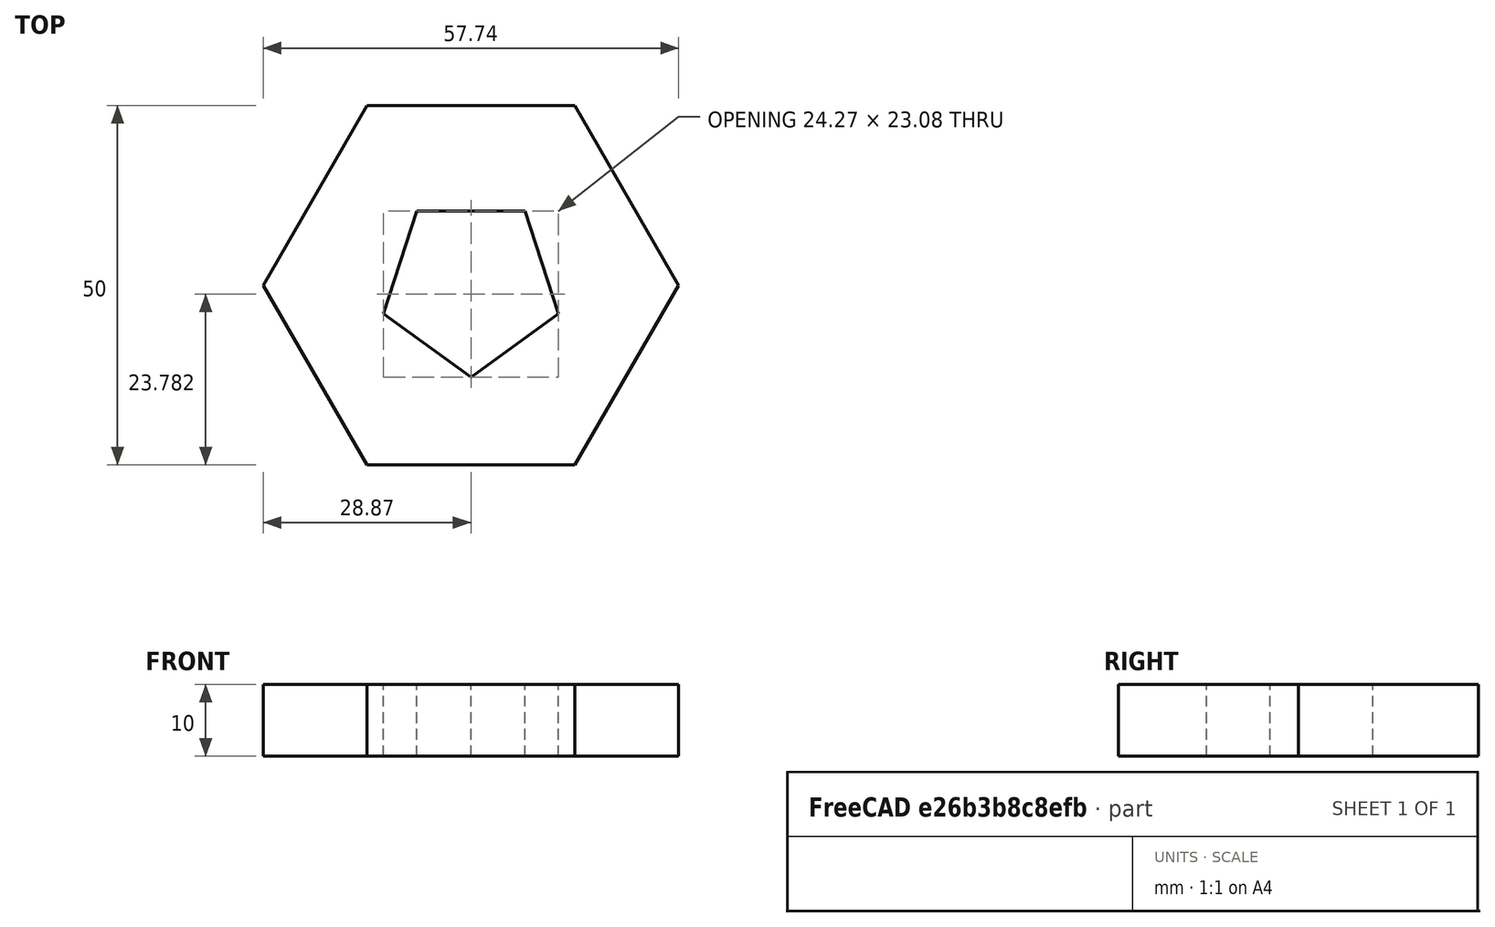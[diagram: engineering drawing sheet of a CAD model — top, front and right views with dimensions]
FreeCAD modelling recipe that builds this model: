
FCSTD DOCUMENT  (FreeCAD 1.0R39109 (Git))
Label: hole_poly
License: All rights reserved
LicenseURL: https://en.wikipedia.org/wiki/All_rights_reserved
objects: Sketcher::SketchObject×1, Part::Extrusion×1
note: 3 computed .brp shape members not serialized (recipe doc carries the construction recipe); baked Part::Feature solids carry a one-line shape summary decoded from their .brp

FEATURE [Sketcher::SketchObject] Sketch
  ArcFitTolerance = 1e-06
  FullyConstrained = true
  MakeInternals = false
  sketch-geometry (13):
    g0: LineSegment StartX=28.8675 StartY=0 StartZ=0 EndX=14.4338 EndY=25 EndZ=0
    g1: LineSegment StartX=14.4338 StartY=25 StartZ=0 EndX=-14.4338 EndY=25 EndZ=0
    g2: LineSegment StartX=-14.4338 StartY=25 StartZ=0 EndX=-28.8675 EndY=3.6e-15 EndZ=0
    g3: LineSegment StartX=-28.8675 StartY=2e-15 StartZ=0 EndX=-14.4338 EndY=-25 EndZ=0
    g4: LineSegment StartX=-14.4338 StartY=-25 StartZ=0 EndX=14.4338 EndY=-25 EndZ=0
    g5: LineSegment StartX=14.4338 StartY=-25 StartZ=0 EndX=28.8675 EndY=0 EndZ=0
    g6: Circle [constr] CenterX=0 CenterY=0 CenterZ=0 NormalX=0 NormalY=0 NormalZ=1 AngleXU=0 Radius=28.8675
    g7: LineSegment StartX=7.5 StartY=10.3229 StartZ=0 EndX=-7.5 EndY=10.3229 EndZ=0
    g8: LineSegment StartX=-7.5 StartY=10.3229 StartZ=0 EndX=-12.1353 EndY=-3.94298 EndZ=0
    g9: LineSegment StartX=-12.1353 StartY=-3.94298 StartZ=0 EndX=4.8e-14 EndY=-12.7598 EndZ=0
    g10: LineSegment StartX=4.78e-14 StartY=-12.7598 StartZ=0 EndX=12.1353 EndY=-3.94298 EndZ=0
    g11: LineSegment StartX=12.1353 StartY=-3.94298 StartZ=0 EndX=7.5 EndY=10.3229 EndZ=0
    g12: Circle [constr] CenterX=0 CenterY=0 CenterZ=0 NormalX=0 NormalY=0 NormalZ=1 AngleXU=0 Radius=12.7598
  constraints (30):
    c: Coincident(g0,g1)
    c: Coincident(g1,g2)
    c: Coincident(g2,g3)
    c: Coincident(g3,g4)
    c: Coincident(g4,g5)
    c: Coincident(g5,g0)
    c: Equal(g0, g1-g5) x5
    c: PointOnObject(g0,g6)
    c: PointOnObject(g1,g6)
    c: PointOnObject(g2,g6)
    c: PointOnObject(g3,g6)
    c: PointOnObject(g4,g6)
    c: PointOnObject(g5,g6)
    c: Coincident(g6,g-1)
    c: PointOnObject(g5,g-1)
    c: Distance(g5,g2) = 50
    c: Coincident(g7,g8)
    c: Coincident(g8,g9)
    c: Coincident(g9,g10)
    c: Coincident(g10,g11)
    c: Coincident(g11,g7)
    c: Equal(g7, g8-g11) x4
    c: PointOnObject(g7,g12)
    c: PointOnObject(g8,g12)
    c: PointOnObject(g9,g12)
    c: PointOnObject(g10,g12)
    c: PointOnObject(g11,g12)
    c: Coincident(g12,g6)
    c: Distance(g9,g9) = 15
    c: Horizontal(g7)
FEATURE [Part::Extrusion] Extrude
  Base = -> Sketch
  Dir = (0,0,1)
  DirMode = 2
  FaceMakerClass = Part::FaceMakerBullseye
  FaceMakerMode = 3
  LengthFwd = 10
  LengthRev = 0
  Solid = true
  Symmetric = false
